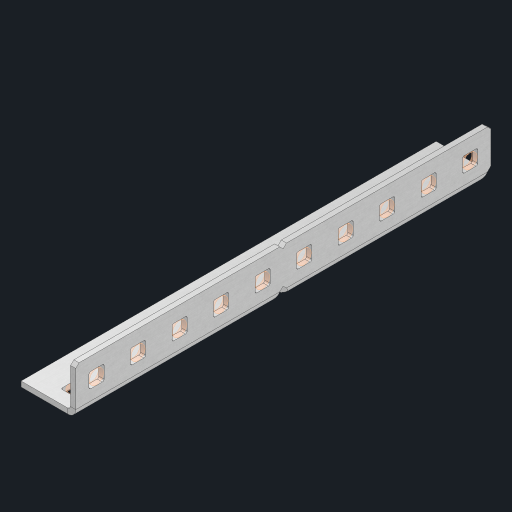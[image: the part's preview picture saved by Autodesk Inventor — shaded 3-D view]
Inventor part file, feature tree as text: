
AUTODESK INVENTOR PART (.ipt)
format: ipt  version: 2023 (Build 270158000, 158)  size: 586,240 bytes
history: native  units: in
note: dims shown in document units (in); Inventor stores cm internally (conversion verified against a paired STEP export)
features: other x25, extrude x19, sheet_metal_op x10, sketch x8, mirror x1, pattern_linear x1, chamfer x1
ambient origin geometry x8: Origin, YZ Plane, XZ Plane, XY Plane, X Axis, Y Axis, Z Axis, Center Point
bodies: Solid1 (feature_tree), Body (feature_tree)
feature tree (65):
  other  "Flange Pattern Plane"
  sheet_metal_op  "Flange Pattern"
  sheet_metal_op  "Body Pattern"
  other  "Arc Length"
  mirror  "Notch Mirror"
  pattern_linear  "Notch Pattern"  Spacing1=0.25in  [1 undecoded]
  chamfer  "End Chamfer"
  extrude  "Half Cut"  Depth=0.0625in
  sketch  "Sketch1"  dims[d0=1.5in]
  other  "Plate1"
  sketch  "Sketch2"  dims[d1=5.0in]
  other  "Plate2"
  sheet_metal_op  "Bend1"
  sheet_metal_op  "Corner1"
  sketch  "Sketch3"  dims[d2=0.0625in]
  other  "Flange Pattern Sketch"
  sketch  "Sketch7"  dims[d3=0.0625in]
  other  "Srf1"
  other  "Srf2"
  sketch  "Sketch8"  dims[d4=0.0312in]
  sketch  "Sketch9"  dims[d5=0.125in]
  other  "Srf91"
  sheet_metal_op  "Body Pattern Sketch"
  other  "Srf92"
  sketch  "Sketch13"  dims[d6=0.0625in]
  sketch  "Sketch14"  dims[d7=0.5in d8=90.0deg d9=0.0312in d10=0.25in d11=0.0625in d12=0.0625in d16=0.182in d17=0.02in d18=0.0625in d19=0.0in d20=0.25in d21=0.25in d46=0.172in d47=1.0in d48=0.0in d49=0.182in d50=0.02in d51=0.25in d52=0.25in d53=0.0625in d54=0.0in d55=0.172in d56=1.0in d57=0.0in d60=3.937in d62=0.5in d63=0.3937in d65=0.5in d85=0.1473in d86=0.1782in d88=0.04in d89=0.0625in d90=0.0in d91=0.04in d92=0.0491in d95=2.5in d96=0.04in d97=0.25in d98=45.0deg d101=0.0in d102=2.497in d131=0.5in d132=3.937in d134=0.5in d139=0.5in]
  other  "Srf856"
  other  "Srf1310"
  other  "Srf1311"
  other  "Srf1312"
  other  "Srf1376"
  other  "Srf1377"
  other  "Srf1728"
  other  "Srf1755"
  other  "Srf1878"
  other  "Srf1879"
  other  "Srf1880"
  other  "Srf1881"
  other  "Srf1942"
  other  "Srf1943"
  other  "Srf1944"
  other  "Srf1945"
  sheet_metal_op  "Flange Stamp"
  sheet_metal_op  "Flange Circle"
  sheet_metal_op  "Body Stamp"
  sheet_metal_op  "Body Circle"
  sheet_metal_op  "Notch"
  extrude  "ExtrusionSrf2"  Depth=0.0625in
  extrude  "ExtrusionSrf92"  Depth=0.5in
  extrude  "ExtrusionSrf856"  Depth=0.02in
  extrude  "ExtrusionSrf1310"  Depth=0.0625in
  extrude  "ExtrusionSrf1311"  TaperAngle=0.0deg  [1 undecoded]
  extrude  "ExtrusionSrf1312"  Depth=0.5in
  extrude  "ExtrusionSrf1376"  Depth=0.5in
  extrude  "ExtrusionSrf1377"  Depth=0.5in
  extrude  "ExtrusionSrf1728"  Depth=0.5in TaperAngle=0.0deg
  extrude  "ExtrusionSrf1755"  Depth=0.5in
  extrude  "ExtrusionSrf1878"  Depth=0.02in
  extrude  "ExtrusionSrf1879"  Depth=0.5in
  extrude  "ExtrusionSrf1880"  Depth=0.5in
  extrude  "ExtrusionSrf1881"  Depth=0.0625in
  extrude  "ExtrusionSrf1942"  TaperAngle=0.0deg  [1 undecoded]
  extrude  "ExtrusionSrf1943"  Depth=0.5in
  extrude  "ExtrusionSrf1944"  Depth=0.5in TaperAngle=0.0deg
  extrude  "ExtrusionSrf1945"  Depth=0.5in
note: 3 required parameter values undecoded (feature->parameter linkage not recoverable at this tier; creation-order binding heuristic only, values carry confidence <= 0.55)
